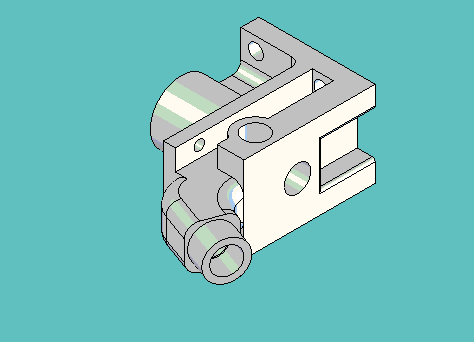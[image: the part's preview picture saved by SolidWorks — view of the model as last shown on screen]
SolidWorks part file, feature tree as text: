
SOLIDWORKS PART (.sldprt)
format: sldprt  version: not decoded by parser v0  size: 1,905,664 bytes
history: native  units: mm
features: sketch x20, boolean_combine x9, cut_extrude x9, extrude x8, fillet x3, material x1, plane x1, revolve x1, chamfer x1, sweep x1 (+11 scaffold rows collapsed)
feature tree (65):
  scaffold x11  (default folders/planes/origin — collapsed)
  material  "Material <not specified>"
  sketch  "Sketch1"  dims[D1=4.7498mm D2=11.43mm D3=11.43mm D4=30.9626mm]
  extrude  "Extrude1"  Depth=41.275mm
  sketch  "Sketch5"  dims[D1=5.6515mm D2=5.6515mm D3=14.097mm]
  extrude  "Extrude7"  Depth=4.7752mm
  boolean_combine  "Combine4"
  sketch  "Sketch6"  dims[D2=7.0358mm D1=20.6502mm]
  extrude  "Extrude8"  Depth=38.1mm
  plane  "Plane1"
  boolean_combine  "Combine5"
  sketch  "Sketch7"  dims[D1=10.16mm]
  extrude  "Extrude10"  Depth=21.6916mm
  boolean_combine  "Combine6"
  sketch  "Sketch8"  dims[D1=6.604mm D2=4.7752mm]
  extrude  "Extrude11"  [1 undecoded]
  boolean_combine  "Combine7"
  sketch  "Sketch9"  dims[c1.D3=6.5278mm c1.D1=28.956mm c1.D2=4.7625mm c2.D1=27.1272mm]
  extrude  "Extrude12"  Depth=38.1mm
  boolean_combine  "Combine8"
  sketch  "Sketch11"  dims[c1.D1=0.381mm c1.D2=3.175mm c2.D1=3.175mm c2.D3=0.254mm c2.D4=7.62mm c2.D2=0.381mm]
  revolve  "Revolve2"  Angle=360deg
  boolean_combine  "Combine11"
  sketch  "Sketch12"  dims[c1.D1=~3.96875mm c1.D2=~3.96875mm c1.D3=3.175mm c1.D7=3.175mm c1.D4=9.525mm c1.D5=7.9248mm c1.D6=7.9248mm c2.D7=26.9748mm c2.D8=26.9748mm c2.D4=26.9875mm c2.D3=7.9248mm c2.D6=9.525mm c2.D5=7.9248mm c3.D8=7.9248mm c3.D9=9.525mm c4.D8=7.9248mm]
  extrude  "Extrude14"  Depth=12.7mm
  boolean_combine  "Combine12"
  chamfer  "Chamfer1"  Distance=0.889mm Angle=15deg
  sketch  "Sketch21"  dims[D1=3.175mm D2=15.875mm]
  cut_extrude  "Cut-Extrude6"  [1 undecoded]
  sketch  "Sketch24"  dims[c1.D2=2.032mm c1.D3=~2.38125mm c1.D4=~2.38125mm c1.D5=3.175mm c1.D1=4.7625mm c2.D3=3.175mm c2.D4=1.5875mm c2.D5=1.5875mm c2.D1=0.0mm]
  cut_extrude  "Cut-Extrude9"  [1 undecoded]
  fillet  "Fillet1"  Radius=2.38125mm
  sketch  "Sketch25"  dims[c1.D2=6.5278mm c1.D1=3.175mm c2.D2=22.225mm c2.D3=6.35mm c3.D2=1.778mm c3.D4=3.175mm c3.D5=7.9375mm c4.D4=31.75mm]
  cut_extrude  "Cut-Extrude10"  Depth=5.55625mm
  sketch  "Sketch26"  dims[D1=0.0mm]
  cut_extrude  "Cut-Extrude11"  Depth=5.55625mm
  sketch  "Sketch27"  dims[D3=~2.778125mm D5=2.7051mm D1=34.925mm D2=8.89mm D4=8.89mm]
  cut_extrude  "Cut-Extrude12"  [1 undecoded]
  sketch  "Sketch29"  dims[D1=0.0mm]
  cut_extrude  "Cut-Extrude14"  Depth=6.35mm
  sketch  "Sketch30"
  sketch  "Sketch31"  dims[c1.D1=~20.20113mm c2.D1=70.0deg c2.D2=12.7mm c2.D3=6.35mm c2.D4=4.953mm c2.D5=4.953mm]
  sweep  "Sweep1"
  sketch  "Sketch32"  dims[c1.D1=9.525mm c1.D4=5.08mm c1.D3=6.35mm c2.D1=~7.666823mm c3.D1=54.0deg c3.D2=~15.09935mm c4.D2=42.0deg c4.D1=5.08mm c5.D2=5.08mm c5.D3=6.35mm c5.D1=~5.87502mm c6.D2=~5.87502mm]
  extrude  "Extrude15"  [1 undecoded]
  boolean_combine  "Combine13"
  boolean_combine  "Combine14"
  sketch  "Sketch33"  dims[D1=7.1374mm]
  cut_extrude  "Cut-Extrude15"  Depth=6.35mm
  sketch  "Sketch34"  dims[D2=10.414mm D3=3.175mm D4=3.175mm D1=0.0mm]
  cut_extrude  "Cut-Extrude16"  Depth=6.35mm
  fillet  "Fillet2"  Radius=3.175mm
  fillet  "Fillet3"  Radius=0.79375mm
  sketch  "Sketch37"  dims[D1=13.5128mm]
  cut_extrude  "Cut-Extrude18"  Depth=1.5875mm
decode coverage: 36 of 52 modeling features carry decoded parameters
note: ~ marks probable driven/reference dimensions
note: 5 parameter values undecoded
summary: no parameter record found for 5 features
note: suppression state not decoded; provenance and decode notes live in map.json
